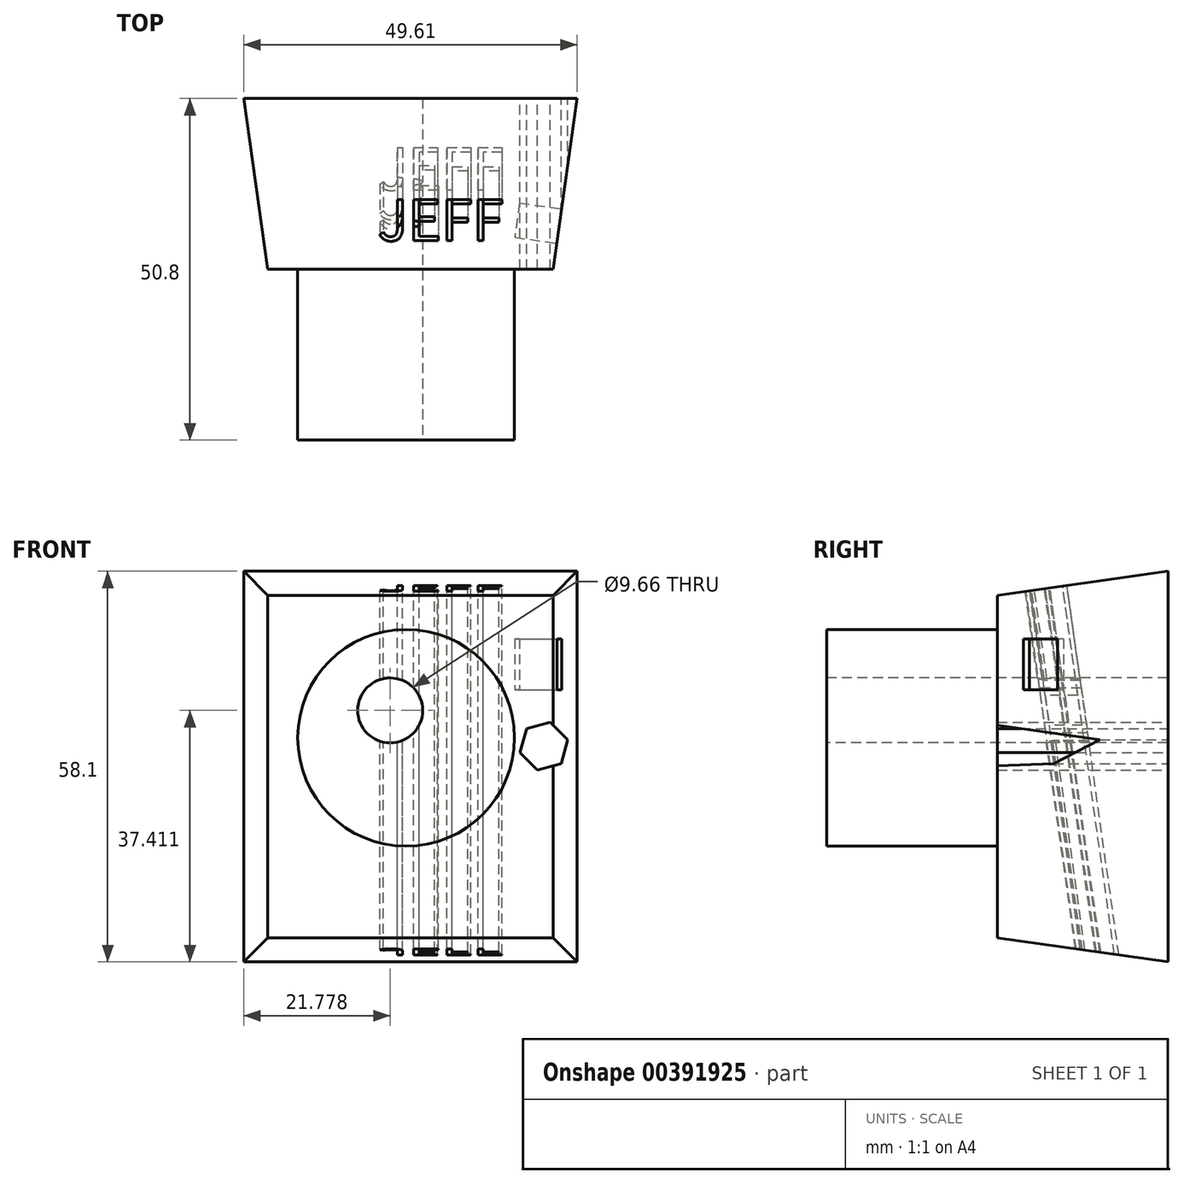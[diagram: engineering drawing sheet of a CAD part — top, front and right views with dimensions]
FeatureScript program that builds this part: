
annotation { "Feature Type Name" : "Feature", "Feature Type Description" : "" }
export const myFeature = defineFeature(function(context is Context, id is Id, definition is map)
    precondition{}
    {
        {
            var Q0;
            Q0=qCreatedBy(makeId("Front.planeOp"),FACE);
            var sketch = newSketch(context, id + "F0", { "sketchPlane" : qUnion([Q0])});
            skLineSegment(sketch, "E0.bottom", {"start": v(54.17, 58.1) * mm, "end": v(4.56, 58.1) * mm});
            skLineSegment(sketch, "E0.top", {"start": v(54.17, 0) * mm, "end": v(4.56, 0) * mm});
            skLineSegment(sketch, "E0.left", {"start": v(54.17, 58.1) * mm, "end": v(54.17, 0) * mm});
            skLineSegment(sketch, "E0.right", {"start": v(4.56, 58.1) * mm, "end": v(4.56, 0) * mm});
            skSolve(sketch);
        }
        {
            var Q0;
            Q0 = qSketchRegion(id + "F0", true);
            extrude(context, id + "F1", {"entities" : qUnion([Q0]), "depth" : 25.4 * mm, "hasDraft" : true, "draftAngle" : 8 * degree, "draftPullDirection" : true});
        }
        {
            var Q0;
            Q0=makeQuery(id+"F1.opExtrude","CAP_FACE",FACE,{"disambiguationData":[OSD([sQuery(id+"F0.wireOp",EDGE,"E0.bottom"),sQuery(id+"F0.wireOp",EDGE,"E0.top"),sQuery(id+"F0.wireOp",EDGE,"E0.left"),sQuery(id+"F0.wireOp",EDGE,"E0.right")])],"isStart":false});
            var sketch = newSketch(context, id + "F2", { "sketchPlane" : qUnion([Q0])});
            skCircle(sketch, "E1", {"center": v(28.71, 33.33) * mm, "radius": 16.13 * mm});
            skSolve(sketch);
        }
        {
            var Q0;
            Q0 = qSketchRegion(id + "F2", true);
            extrude(context, id + "F3", {"entities" : qUnion([Q0]), "operationType" : NewBodyOperationType.ADD, "depth" : 25.4 * mm});
        }
        {
            var Q0;
            Q0=makeQuery(id+"F3.opExtrude","CAP_FACE",FACE,{"disambiguationData":[OSD([sQuery(id+"F2.wireOp",EDGE,"E1")])],"isStart":false});
            var sketch = newSketch(context, id + "F4", { "sketchPlane" : qUnion([Q0])});
            skCircle(sketch, "E2", {"center": v(26.34, 37.41) * mm, "radius": 4.83 * mm});
            skSolve(sketch);
        }
        {
            var Q0;
            Q0 = qSketchRegion(id + "F4", true);
            extrude(context, id + "F5", {"entities" : qUnion([Q0]), "operationType" : NewBodyOperationType.REMOVE, "endBound" : BoundingType.THROUGH_ALL, "oppositeDirection" : true, "depth" : 25.4 * mm});
        }
        {
            var Q0;
            Q0=qCreatedBy(makeId("Front.planeOp"),FACE);
            var sketch = newSketch(context, id + "F6", { "sketchPlane" : qUnion([Q0])});
            skCircle(sketch, "E3.cCircle", {"center": v(49.2, 32.1) * mm, "radius": 3.67 * mm, "construction": true});
            skLineSegment(sketch, "E3.0", {"start": v(50.17, 35.63) * mm, "end": v(52.75, 33.03) * mm});
            skLineSegment(sketch, "E3.1", {"start": v(52.75, 33.03) * mm, "end": v(51.78, 29.5) * mm});
            skLineSegment(sketch, "E3.2", {"start": v(51.78, 29.5) * mm, "end": v(48.24, 28.56) * mm});
            skLineSegment(sketch, "E3.3", {"start": v(48.24, 28.56) * mm, "end": v(45.66, 31.17) * mm});
            skLineSegment(sketch, "E3.4", {"start": v(45.66, 31.17) * mm, "end": v(46.62, 34.7) * mm});
            skLineSegment(sketch, "E3.5", {"start": v(46.62, 34.7) * mm, "end": v(50.17, 35.63) * mm});
            skSolve(sketch);
        }
        {
            var Q0;
            Q0 = qSketchRegion(id + "F6", true);
            extrude(context, id + "F7", {"entities" : qUnion([Q0]), "operationType" : NewBodyOperationType.REMOVE, "endBound" : BoundingType.THROUGH_ALL, "depth" : 25.4 * mm});
        }
        {
            var Q0;
            Q0=makeQuery(id+"F1.opExtrude","SWEPT_FACE",FACE,{"disambiguationData":[OSD([sQuery(id+"F0.wireOp",EDGE,"E0.left")])]});
            var sketch = newSketch(context, id + "F8", { "sketchPlane" : qUnion([Q0])});
            skLineSegment(sketch, "E4.bottom", {"start": v(-9.02, 48.06) * mm, "end": v(-14.19, 48.06) * mm});
            skLineSegment(sketch, "E4.top", {"start": v(-9.02, 40.45) * mm, "end": v(-14.19, 40.45) * mm});
            skLineSegment(sketch, "E4.left", {"start": v(-9.02, 48.06) * mm, "end": v(-9.02, 40.45) * mm});
            skLineSegment(sketch, "E4.right", {"start": v(-14.19, 48.06) * mm, "end": v(-14.19, 40.45) * mm});
            skSolve(sketch);
        }
        {
            var Q0;
            Q0 = qSketchRegion(id + "F8", true);
            extrude(context, id + "F9", {"entities" : qUnion([Q0]), "operationType" : NewBodyOperationType.REMOVE, "oppositeDirection" : true, "depth" : 6.35 * mm});
        }
        {
            var Q0;
            Q0=makeQuery(id+"F1.opExtrude","SWEPT_FACE",FACE,{"disambiguationData":[OSD([sQuery(id+"F0.wireOp",EDGE,"E0.bottom")])]});
            var sketch = newSketch(context, id + "F10", { "sketchPlane" : qUnion([Q0])});
            skText(sketch, "E5", { "text": "JEFF", "fontName": "NotoSansCJKjp-Regular.otf"});
            const initialGuessF10  = {"E5": [0.0245, -0.01324, 1, 0, 0.00605]};
            skSetInitialGuess(sketch, initialGuessF10);
            skSolve(sketch);
        }
        {
            var Q0;
            Q0 = qSketchRegion(id + "F10", true);
            extrude(context, id + "F11", {"entities" : qUnion([Q0]), "operationType" : NewBodyOperationType.REMOVE, "endBound" : BoundingType.THROUGH_ALL, "oppositeDirection" : true, "depth" : 25.4 * mm});
        }
    });
